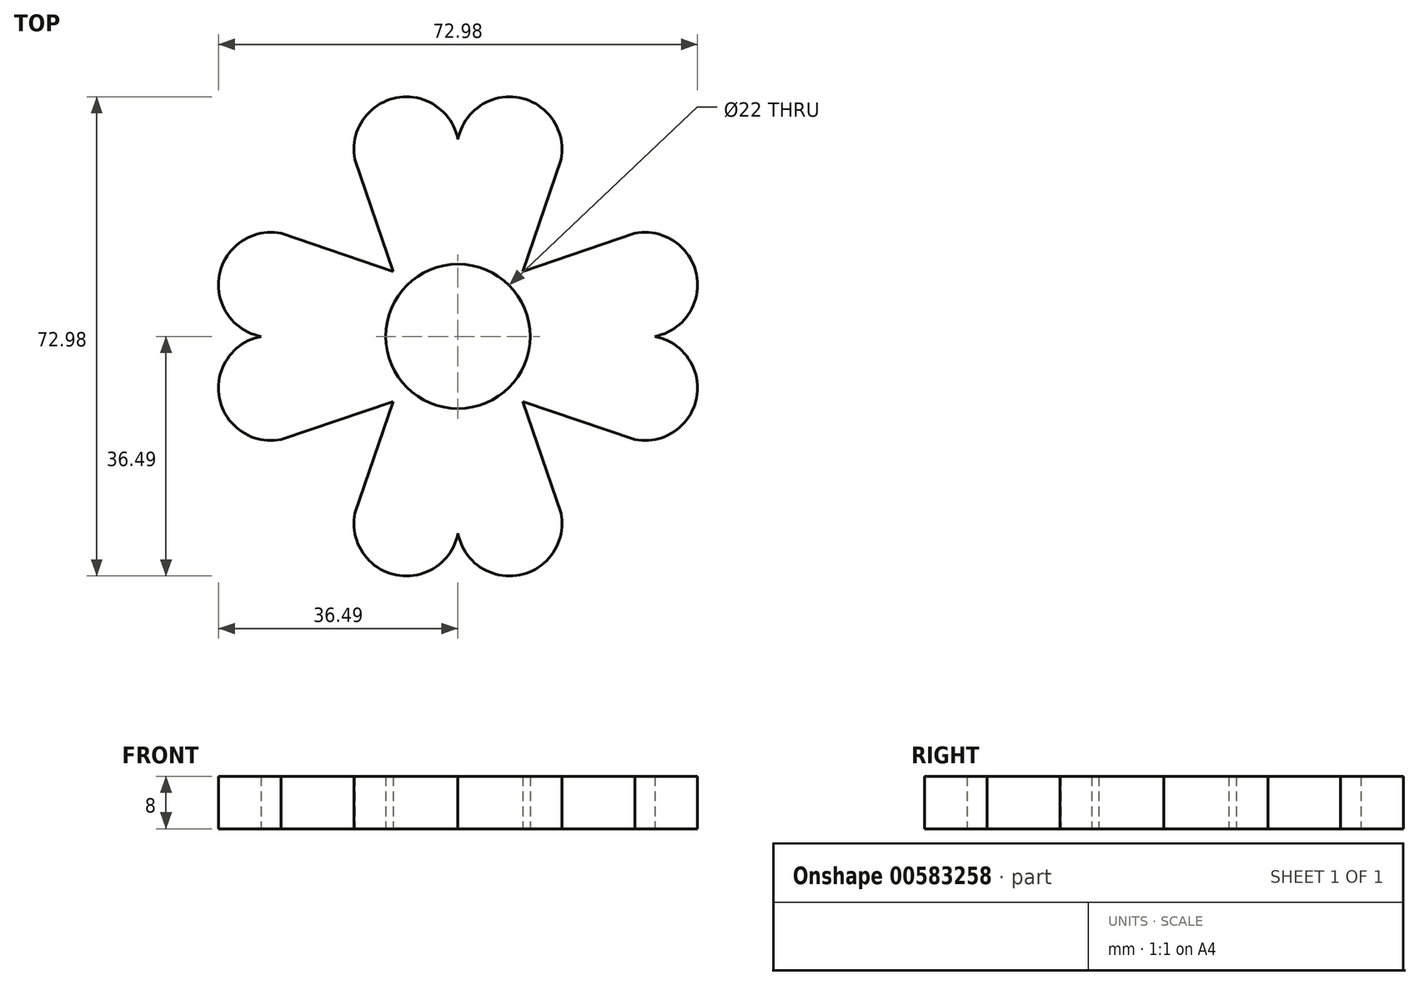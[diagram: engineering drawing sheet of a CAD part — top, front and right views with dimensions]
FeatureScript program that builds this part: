
annotation { "Feature Type Name" : "Feature", "Feature Type Description" : "" }
export const myFeature = defineFeature(function(context is Context, id is Id, definition is map)
    precondition{}
    {
        {
            var Q0;
            Q0=qCreatedBy(makeId("Top.planeOp"),FACE);
            var sketch = newSketch(context, id + "F0", { "sketchPlane" : qUnion([Q0])});
            skCircle(sketch, "E0", {"center": v(0, 0) * mm, "radius": 11 * mm});
            skLineSegment(sketch, "E1", {"start": v(0, 0) * mm, "end": v(0, 30) * mm, "construction": true});
            skCircle(sketch, "E2", {"center": v(0, 0) * mm, "radius": 14 * mm});
            skLineSegment(sketch, "E3", {"start": v(0, 0) * mm, "end": v(9.9, 9.9) * mm, "construction": true});
            skLineSegment(sketch, "E4", {"start": v(9.9, 9.9) * mm, "end": v(15.7, 26.94) * mm});
            skArc(sketch, "E5", {"start": v(15.7, 26.94) * mm, "mid": v(9.39, 36.35) * mm, "end": v(0, 30) * mm});
            skLineSegment(sketch, "E6.MirrorCS", {"start": v(-9.9, 9.9) * mm, "end": v(-15.7, 26.94) * mm});
            skArc(sketch, "E7.MirrorCS", {"start": v(-15.7, 26.94) * mm, "mid": v(-9.39, 36.35) * mm, "end": v(0, 30) * mm});
            skLineSegment(sketch, "E8.MirrorCS", {"start": v(9.9, 9.9) * mm, "end": v(26.94, 15.7) * mm});
            skArc(sketch, "E9.MirrorCS", {"start": v(26.94, 15.7) * mm, "mid": v(36.35, 9.39) * mm, "end": v(30, 0) * mm});
            skArc(sketch, "E10.MirrorCS", {"start": v(26.94, -15.7) * mm, "mid": v(36.35, -9.39) * mm, "end": v(30, 0) * mm});
            skLineSegment(sketch, "E11.MirrorCS", {"start": v(9.9, -9.9) * mm, "end": v(26.94, -15.7) * mm});
            skLineSegment(sketch, "E12.MirrorCS", {"start": v(-9.9, -9.9) * mm, "end": v(-26.94, -15.7) * mm});
            skLineSegment(sketch, "E13.MirrorCS", {"start": v(-9.9, 9.9) * mm, "end": v(-26.94, 15.7) * mm});
            skArc(sketch, "E14.MirrorCS", {"start": v(-26.94, 15.7) * mm, "mid": v(-36.35, 9.39) * mm, "end": v(-30, 0) * mm});
            skArc(sketch, "E15.MirrorCS", {"start": v(-26.94, -15.7) * mm, "mid": v(-36.35, -9.39) * mm, "end": v(-30, 0) * mm});
            skLineSegment(sketch, "E16", {"start": v(0, 0) * mm, "end": v(47.08, 0) * mm, "construction": true});
            skLineSegment(sketch, "E17.MirrorCS", {"start": v(-9.9, -9.9) * mm, "end": v(-15.7, -26.94) * mm});
            skLineSegment(sketch, "E18.MirrorCS", {"start": v(9.9, -9.9) * mm, "end": v(15.7, -26.94) * mm});
            skArc(sketch, "E19.MirrorCS", {"start": v(15.7, -26.94) * mm, "mid": v(9.39, -36.35) * mm, "end": v(0, -30) * mm});
            skArc(sketch, "E20.MirrorCS", {"start": v(-15.7, -26.94) * mm, "mid": v(-9.39, -36.35) * mm, "end": v(0, -30) * mm});
            skSolve(sketch);
        }
        {
            var Q0;
            Q0=makeQuery(id+"F0.imprint","IMPRINT",FACE,{"disambiguationData":[TD([[makeQuery(id+"F0.imprint","IMPRINT",EDGE,{"derivedFrom":sQuery(id+"F0.wireOp",EDGE,"E0")}),-1.0]])]});
            var Q1;
            {var subQ1=sQuery(id+"F0.wireOp",EDGE,"E12.MirrorCS");Q1=makeQuery(id+"F0.imprint","IMPRINT",FACE,{"disambiguationData":[TD([[makeQuery(id+"F0.imprint","IMPRINT",EDGE,{"derivedFrom":subQ1}),-1.0]])]});}
            var Q2;
            {var subQ1=sQuery(id+"F0.wireOp",EDGE,"E4");Q2=makeQuery(id+"F0.imprint","IMPRINT",FACE,{"disambiguationData":[TD([[makeQuery(id+"F0.imprint","IMPRINT",EDGE,{"derivedFrom":subQ1}),1.0]])]});}
            var Q3;
            {var subQ0=sQuery(id+"F0.wireOp",EDGE,"E8.MirrorCS");Q3=makeQuery(id+"F0.imprint","IMPRINT",FACE,{"disambiguationData":[TD([[makeQuery(id+"F0.imprint","IMPRINT",EDGE,{"derivedFrom":subQ0}),-1.0]])]});}
            var Q4;
            {var subQ0=sQuery(id+"F0.wireOp",EDGE,"E17.MirrorCS");Q4=makeQuery(id+"F0.imprint","IMPRINT",FACE,{"disambiguationData":[TD([[makeQuery(id+"F0.imprint","IMPRINT",EDGE,{"derivedFrom":subQ0}),1.0]])]});}
            extrude(context, id + "F1", {"entities" : qUnion([Q0, Q1, Q2, Q3, Q4]), "depth" : 8 * mm, "offsetDistance" : 25 * mm});
        }
    });
